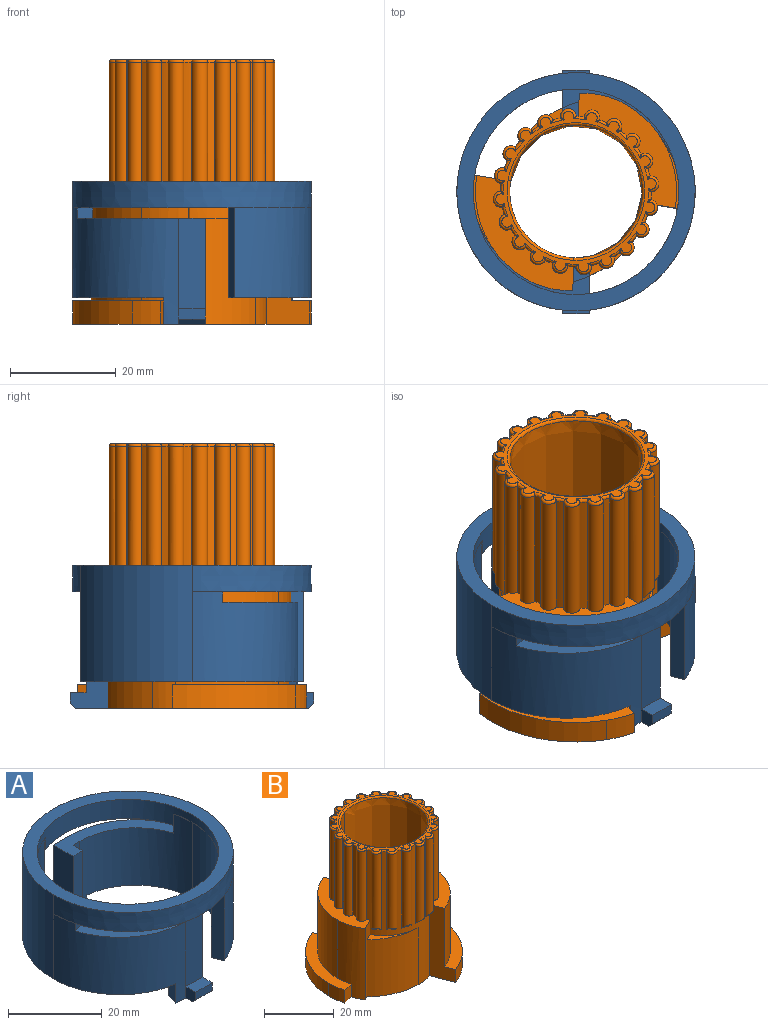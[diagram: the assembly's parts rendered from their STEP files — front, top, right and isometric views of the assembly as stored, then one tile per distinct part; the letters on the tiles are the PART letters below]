
ASSEMBLY  parts=2 mates=1
PART A: 47 faces, bbox 45x46x27 mm
  f0: plane 20x2.78mm, normal (-1,0.03,0), area 55.7mm2, adj f1,f9,f14,f44
  f1: plane 8x7.81mm, normal (0,0,-1), area 40.7mm2, adj f0,f8,f9,f10,f12,f16,f19,f44
  f2: plane 20x2.78mm, normal (1,-0.03,0), area 55.7mm2, adj f3,f27,f32,f39
  f3: plane 8x7.81mm, normal (0,0,-1), area 40.7mm2, adj f2,f26,f27,f28,f30,f34,f37,f39
  f4: plane 30.51x22.49mm, normal (0,0,-1), area 108.7mm2, adj f12,f15,f21,f22,f24,f41
  f5: plane 30.51x22.51mm, normal (0,0,-1), area 108.7mm2, adj f6,f21,f22,f30,f33,f43
  f6: plane 17x2.8mm, normal (0.93,0.36,0), area 51mm2, adj f5,f7,f13,f17
  f7: cylinder r=19.5mm len=20mm, axis (0,0,-1), area 470.8mm2, adj f6,f8,f17,f42,f43
  f8: cylinder r=17mm len=25mm, axis (0,0,-1), area 436.2mm2, adj f1,f7,f9,f14,f15,f16,f17,f22
  f9: plane 20x2mm, normal (0,1,0), area 40mm2, adj f0,f1,f8,f14
  f10: plane 20x9mm, normal (1,0,0), area 128.5mm2, adj f1,f11,f14,f18,f20,f44,f46
  f11: plane 17x5mm, normal (0,-1,0), area 85mm2, adj f10,f12,f14,f20
  f12: cylinder r=20mm len=22mm, axis (0,0,-1), area 497.1mm2, adj f1,f4,f11,f13,f14,f15,f16,f17
  f13: cylinder r=22.5mm len=22mm, axis (0,0,-1), area 597.6mm2, adj f6,f12,f17,f21,f23
  f14: plane 24.14x14.98mm, normal (0,0,1), area 94.1mm2, adj f0,f8,f9,f10,f11,f12,f15,f44
  f15: plane 2.9x2mm, normal (0.26,-0.97,0), area 6mm2, adj f4,f8,f12,f14
  f16: plane 5x2.92mm, normal (-0.97,0.26,0), area 15.1mm2, adj f1,f8,f12,f17
  f17: plane 40.83x17.98mm, normal (0,0,-1), area 156mm2, adj f6,f7,f8,f12,f13,f16
  f18: plane 5x2mm, normal (0,-1,0), area 10mm2, adj f10,f19,f20,f46
  f19: plane 3x3mm, normal (-1,0,0), area 8.5mm2, adj f1,f12,f18,f20,f46
  f20: plane 5x3mm, normal (0,0,1), area 15mm2, adj f10,f11,f18,f19
  f21: extruded ~44.99x44.97mm, area 571.1mm2, adj f4,f5,f12,f13,f23,f31
  f22: cylinder r=19.4mm len=38.81mm, axis (0,0,-1), area 438.5mm2, adj f4,f5,f8,f23,f26,f40,f41,f42
  f23: plane 45.01x45.01mm, normal (0,0,1), area 407.9mm2, adj f13,f21,f22
  f24: plane 17x2.8mm, normal (-0.93,-0.36,0), area 51mm2, adj f4,f25,f31,f35
  f25: cylinder r=19.5mm len=20mm, axis (0,0,-1), area 470.8mm2, adj f24,f26,f35,f40,f41
  f26: cylinder r=17mm len=25mm, axis (0,0,-1), area 436.2mm2, adj f3,f22,f25,f27,f32,f33,f34,f35
  f27: plane 20x2mm, normal (0,-1,0), area 40mm2, adj f2,f3,f26,f32
  f28: plane 20x9mm, normal (-1,0,0), area 128.5mm2, adj f3,f29,f32,f36,f38,f39,f45
  f29: plane 17x5mm, normal (0,1,0), area 85mm2, adj f28,f30,f32,f38
  f30: cylinder r=20mm len=22mm, axis (0,0,-1), area 497.1mm2, adj f3,f5,f29,f31,f32,f33,f34,f35
  f31: cylinder r=22.5mm len=21.03mm, axis (0,0,-1), area 461.8mm2, adj f21,f24,f30,f35
  f32: plane 24.14x14.98mm, normal (0,0,1), area 94.1mm2, adj f2,f26,f27,f28,f29,f30,f33,f39
  f33: plane 2.9x2mm, normal (-0.26,0.97,0), area 6mm2, adj f5,f26,f30,f32
  f34: plane 5x2.92mm, normal (0.97,-0.26,0), area 15.1mm2, adj f3,f26,f30,f35
  f35: plane 40.83x17.98mm, normal (0,0,-1), area 156mm2, adj f24,f25,f26,f30,f31,f34
  f36: plane 5x2mm, normal (0,1,0), area 10mm2, adj f28,f37,f38,f45
  f37: plane 3x3mm, normal (1,0,0), area 8.5mm2, adj f3,f30,f36,f38,f45
  f38: plane 5x3mm, normal (0,0,1), area 15mm2, adj f28,f29,f36,f37
  f39: cylinder r=14.22mm len=20mm, axis (0,0,-1), area 58.6mm2, adj f2,f3,f28,f32
  f40: plane 23.25x12.6mm, normal (0,0,-1), area 2.6mm2, adj f22,f25,f26,f41
  f41: plane 3x0.09mm, normal (0.93,0.36,0), area 0.3mm2, adj f4,f22,f25,f40
  f42: plane 23.25x12.6mm, normal (0,0,-1), area 2.6mm2, adj f7,f8,f22,f43
  f43: plane 3x0.09mm, normal (-0.93,-0.36,0), area 0.3mm2, adj f5,f7,f22,f42
  f44: cylinder r=14.22mm len=20mm, axis (0,0,-1), area 58.6mm2, adj f0,f1,f10,f14
  f45: plane 5x1mm, normal (0,0.71,-0.71), area 7.1mm2, adj f3,f28,f36,f37
  f46: plane 5x1mm, normal (0,-0.71,-0.71), area 7.1mm2, adj f1,f10,f18,f19
PART B: 111 faces, bbox 45x42.1x50 mm
  f0: cylinder r=14.22mm len=24.5mm, axis (0,0,-1), area 35.9mm2, adj f25,f57,f58,f104
  f1: cylinder r=14.22mm len=24.5mm, axis (0,0,-1), area 35.9mm2, adj f25,f56,f57,f100
  f2: cylinder r=14.22mm len=24.5mm, axis (0,0,-1), area 35.9mm2, adj f25,f55,f56,f96
  f3: cylinder r=14.22mm len=24.5mm, axis (0,0,-1), area 35.9mm2, adj f25,f54,f55,f92
  f4: cylinder r=14.22mm len=24.5mm, axis (0,0,-1), area 35.9mm2, adj f25,f53,f54,f88
  f5: cylinder r=14.22mm len=49.5mm, axis (0,0,-1), area 351.2mm2, adj f12,f21,f24,f25,f37,f38,f48,f49
  f6: cylinder r=14.22mm len=24.5mm, axis (0,0,-1), area 35.9mm2, adj f14,f47,f48,f73
  f7: cylinder r=14.22mm len=24.5mm, axis (0,0,-1), area 35.9mm2, adj f14,f46,f47,f77
  f8: cylinder r=14.22mm len=24.5mm, axis (0,0,-1), area 35.9mm2, adj f14,f45,f46,f81
  f9: cylinder r=14.22mm len=24.5mm, axis (0,0,-1), area 35.9mm2, adj f14,f44,f45,f85
  f10: cylinder r=14.22mm len=24.5mm, axis (0,0,-1), area 35.9mm2, adj f14,f43,f44,f89
  f11: cylinder r=14.22mm len=49.5mm, axis (0,0,-1), area 351.2mm2, adj f13,f14,f21,f23,f35,f36,f39,f40
  f12: plane 25x7.74mm, normal (0.93,0.36,0), area 132.1mm2, adj f5,f14,f15,f20,f21,f22,f48,f63
  f13: plane 25x3.91mm, normal (0.47,-0.88,0), area 55.2mm2, adj f11,f14,f17,f21,f35,f36
  f14: plane 26.61x13.48mm, normal (0,0,1), area 115.2mm2, adj f6,f7,f8,f9,f10,f11,f12,f13
  f15: plane 26.83x15.74mm, normal (0,0,1), area 106.7mm2, adj f12,f17,f18,f19,f20,f22
  f16: cylinder r=12.5mm len=49.5mm, axis (0,0,-1), area 1052.8mm2, adj f21,f33,f110
  f17: cylinder r=16.5mm len=25mm, axis (0,0,-1), area 211.2mm2, adj f13,f14,f15,f18,f21,f22
  f18: plane 4.5x3.38mm, normal (0.26,-0.97,0), area 15.8mm2, adj f15,f17,f19,f21
  f19: cylinder r=20mm len=5.8mm, axis (0,0,-1), area 26.5mm2, adj f15,f18,f20,f21
  f20: cylinder r=22.5mm len=21.03mm, axis (0,0,-1), area 122.2mm2, adj f12,f15,f19,f21
  f21: plane 45x42.06mm, normal (0,0,-1), area 655.8mm2, adj f5,f11,f12,f13,f16,f17,f18,f19
  f22: cylinder r=19mm len=20.5mm, axis (0,0,-1), area 470.2mm2, adj f12,f14,f15,f17
  f23: plane 25x7.74mm, normal (-0.93,-0.36,0), area 132.1mm2, adj f11,f21,f25,f26,f31,f32,f58,f68
  f24: plane 25x3.91mm, normal (-0.47,0.88,0), area 55.2mm2, adj f5,f21,f25,f28,f37,f38
  f25: plane 26.61x13.48mm, normal (0,0,1), area 115.2mm2, adj f0,f1,f2,f3,f4,f5,f23,f24
  f26: plane 26.83x15.74mm, normal (0,0,1), area 106.7mm2, adj f23,f28,f29,f30,f31,f32
  f27: cylinder r=12.5mm len=25mm, axis (0,0,-1), area 531.7mm2, adj f21,f33
  f28: cylinder r=16.5mm len=25mm, axis (0,0,-1), area 211.2mm2, adj f21,f24,f25,f26,f29,f32
  f29: plane 4.5x3.38mm, normal (-0.26,0.97,0), area 15.8mm2, adj f21,f26,f28,f30
  f30: cylinder r=20mm len=5.8mm, axis (0,0,-1), area 26.5mm2, adj f21,f26,f29,f31
  f31: cylinder r=22.5mm len=21.03mm, axis (0,0,-1), area 122.2mm2, adj f21,f23,f26,f30
  f32: cylinder r=19mm len=20.5mm, axis (0,0,-1), area 470.2mm2, adj f23,f25,f26,f28
  f33: extruded ~49.5x24.94mm, area 2303.3mm2, adj f16,f21,f27,f109
  f34: plane 30.44x30.44mm, normal (0,0,1), area 111.6mm2, adj f69,f70,f71,f72,f73,f74,f75,f76
  f35: plane 14.55x7.47mm, normal (0,0,1), area 15mm2, adj f11,f13,f36
  f36: cylinder r=21.29mm len=20mm, axis (0,0,-1), area 323.7mm2, adj f11,f13,f21,f35
  f37: plane 14.55x7.47mm, normal (0,0,1), area 15mm2, adj f5,f24,f38
  f38: cylinder r=21.29mm len=20mm, axis (0,0,-1), area 323.7mm2, adj f5,f21,f24,f37
  f39: cylinder r=1.5mm len=27.5mm, axis (0,0,1), area 129.3mm2, adj f11,f67,f107
  f40: cylinder r=1.5mm len=27.5mm, axis (0,0,1), area 129.3mm2, adj f11,f66,f103
  f41: cylinder r=1.5mm len=27.5mm, axis (0,0,1), area 129.3mm2, adj f11,f65,f99
  f42: cylinder r=1.5mm len=27.5mm, axis (0,0,1), area 129.3mm2, adj f11,f64,f95
  f43: cylinder r=1.5mm len=24.5mm, axis (0,0,1), area 119.3mm2, adj f10,f11,f14,f91
  f44: cylinder r=1.5mm len=24.5mm, axis (0,0,1), area 119.3mm2, adj f9,f10,f14,f87
  f45: cylinder r=1.5mm len=24.5mm, axis (0,0,1), area 119.3mm2, adj f8,f9,f14,f83
  f46: cylinder r=1.5mm len=24.5mm, axis (0,0,1), area 119.3mm2, adj f7,f8,f14,f79
  f47: cylinder r=1.5mm len=24.5mm, axis (0,0,1), area 119.3mm2, adj f6,f7,f14,f75
  f48: cylinder r=1.5mm len=27.5mm, axis (0,0,1), area 125.6mm2, adj f5,f6,f12,f14,f63,f71
  f49: cylinder r=1.5mm len=27.5mm, axis (0,0,1), area 129.3mm2, adj f5,f62,f70
  f50: cylinder r=1.5mm len=27.5mm, axis (0,0,1), area 129.3mm2, adj f5,f61,f74
  f51: cylinder r=1.5mm len=27.5mm, axis (0,0,1), area 129.3mm2, adj f5,f60,f78
  f52: cylinder r=1.5mm len=27.5mm, axis (0,0,1), area 129.3mm2, adj f5,f59,f82
  f53: cylinder r=1.5mm len=24.5mm, axis (0,0,1), area 119.3mm2, adj f4,f5,f25,f86
  f54: cylinder r=1.5mm len=24.5mm, axis (0,0,1), area 119.3mm2, adj f3,f4,f25,f90
  f55: cylinder r=1.5mm len=24.5mm, axis (0,0,1), area 119.3mm2, adj f2,f3,f25,f94
  f56: cylinder r=1.5mm len=24.5mm, axis (0,0,1), area 119.3mm2, adj f1,f2,f25,f98
  f57: cylinder r=1.5mm len=24.5mm, axis (0,0,1), area 119.3mm2, adj f0,f1,f25,f102
  f58: cylinder r=1.5mm len=27.5mm, axis (0,0,1), area 125.6mm2, adj f0,f11,f23,f25,f68,f106
  f59: cone r=16.22mm half-angle=45deg, axis (0,0,1), area 5.1mm2, adj f5,f52
  f60: cone r=16.22mm half-angle=45deg, axis (0,0,1), area 5.1mm2, adj f5,f51
  f61: cone r=16.22mm half-angle=45deg, axis (0,0,1), area 5.1mm2, adj f5,f50
  f62: cone r=16.22mm half-angle=45deg, axis (0,0,1), area 5.1mm2, adj f5,f49
  f63: cone r=16.22mm half-angle=45deg, axis (0,0,1), area 4.1mm2, adj f5,f12,f48
  f64: cone r=16.22mm half-angle=45deg, axis (0,0,1), area 5.1mm2, adj f11,f42
  f65: cone r=16.22mm half-angle=45deg, axis (0,0,1), area 5.1mm2, adj f11,f41
  f66: cone r=16.22mm half-angle=45deg, axis (0,0,1), area 5.1mm2, adj f11,f40
  f67: cone r=16.22mm half-angle=45deg, axis (0,0,1), area 5.1mm2, adj f11,f39
  f68: cone r=16.22mm half-angle=45deg, axis (0,0,1), area 4.1mm2, adj f11,f23,f58
  f69: torus R=13.72mm, axis (0,0,1), area 1.6mm2, adj f5,f34,f70,f71
  f70: torus R=1mm, axis (0,0,1), area 3.8mm2, adj f34,f49,f69,f72
  f71: torus R=1mm, axis (0,0,1), area 3.8mm2, adj f34,f48,f69,f73
  f72: torus R=13.72mm, axis (0,0,1), area 1.6mm2, adj f5,f34,f70,f74
  f73: torus R=13.72mm, axis (0,0,1), area 1.6mm2, adj f6,f34,f71,f75
  f74: torus R=1mm, axis (0,0,1), area 3.8mm2, adj f34,f50,f72,f76
  f75: torus R=1mm, axis (0,0,1), area 3.8mm2, adj f34,f47,f73,f77
  f76: torus R=13.72mm, axis (0,0,1), area 1.6mm2, adj f5,f34,f74,f78
  f77: torus R=13.72mm, axis (0,0,1), area 1.6mm2, adj f7,f34,f75,f79
  f78: torus R=1mm, axis (0,0,1), area 3.8mm2, adj f34,f51,f76,f80
  f79: torus R=1mm, axis (0,0,1), area 3.8mm2, adj f34,f46,f77,f81
  f80: torus R=13.72mm, axis (0,0,1), area 1.6mm2, adj f5,f34,f78,f82
  f81: torus R=13.72mm, axis (0,0,1), area 1.6mm2, adj f8,f34,f79,f83
  f82: torus R=1mm, axis (0,0,1), area 3.8mm2, adj f34,f52,f80,f84
  f83: torus R=1mm, axis (0,0,1), area 3.8mm2, adj f34,f45,f81,f85
  f84: torus R=13.72mm, axis (0,0,1), area 1.6mm2, adj f5,f34,f82,f86
  f85: torus R=13.72mm, axis (0,0,1), area 1.6mm2, adj f9,f34,f83,f87
  f86: torus R=1mm, axis (0,0,1), area 3.8mm2, adj f34,f53,f84,f88
  f87: torus R=1mm, axis (0,0,1), area 3.8mm2, adj f34,f44,f85,f89
  f88: torus R=13.72mm, axis (0,0,1), area 1.6mm2, adj f4,f34,f86,f90
  f89: torus R=13.72mm, axis (0,0,1), area 1.6mm2, adj f10,f34,f87,f91
  f90: torus R=1mm, axis (0,0,1), area 3.8mm2, adj f34,f54,f88,f92
  f91: torus R=1mm, axis (0,0,1), area 3.8mm2, adj f34,f43,f89,f93
  f92: torus R=13.72mm, axis (0,0,1), area 1.6mm2, adj f3,f34,f90,f94
  f93: torus R=13.72mm, axis (0,0,1), area 1.6mm2, adj f11,f34,f91,f95
  f94: torus R=1mm, axis (0,0,1), area 3.8mm2, adj f34,f55,f92,f96
  f95: torus R=1mm, axis (0,0,1), area 3.8mm2, adj f34,f42,f93,f97
  f96: torus R=13.72mm, axis (0,0,1), area 1.6mm2, adj f2,f34,f94,f98
  f97: torus R=13.72mm, axis (0,0,1), area 1.6mm2, adj f11,f34,f95,f99
  f98: torus R=1mm, axis (0,0,1), area 3.8mm2, adj f34,f56,f96,f100
  f99: torus R=1mm, axis (0,0,1), area 3.8mm2, adj f34,f41,f97,f101
  f100: torus R=13.72mm, axis (0,0,1), area 1.6mm2, adj f1,f34,f98,f102
  f101: torus R=13.72mm, axis (0,0,1), area 1.6mm2, adj f11,f34,f99,f103
  f102: torus R=1mm, axis (0,0,1), area 3.8mm2, adj f34,f57,f100,f104
  f103: torus R=1mm, axis (0,0,1), area 3.8mm2, adj f34,f40,f101,f105
  f104: torus R=13.72mm, axis (0,0,1), area 1.6mm2, adj f0,f34,f102,f106
  f105: torus R=13.72mm, axis (0,0,1), area 1.6mm2, adj f11,f34,f103,f107
  f106: torus R=1mm, axis (0,0,1), area 3.8mm2, adj f34,f58,f104,f108
  f107: torus R=1mm, axis (0,0,1), area 3.8mm2, adj f34,f39,f105,f108
  f108: torus R=13.72mm, axis (0,0,1), area 1.6mm2, adj f11,f34,f106,f107
  f109: bspline ~26.01x24.64mm, area 45.6mm2, adj f33,f34,f110
  f110: torus R=13mm, axis (0,0,1), area 16.9mm2, adj f16,f34,f109
PLACE A at identity fixed
PLACE B rot(axis=(0,0,1),59.8deg) t=(0,0,0)mm
MATE revolute B.f27 <-> A.f39  axis (0,0,-1) through (0,0,0)mm
